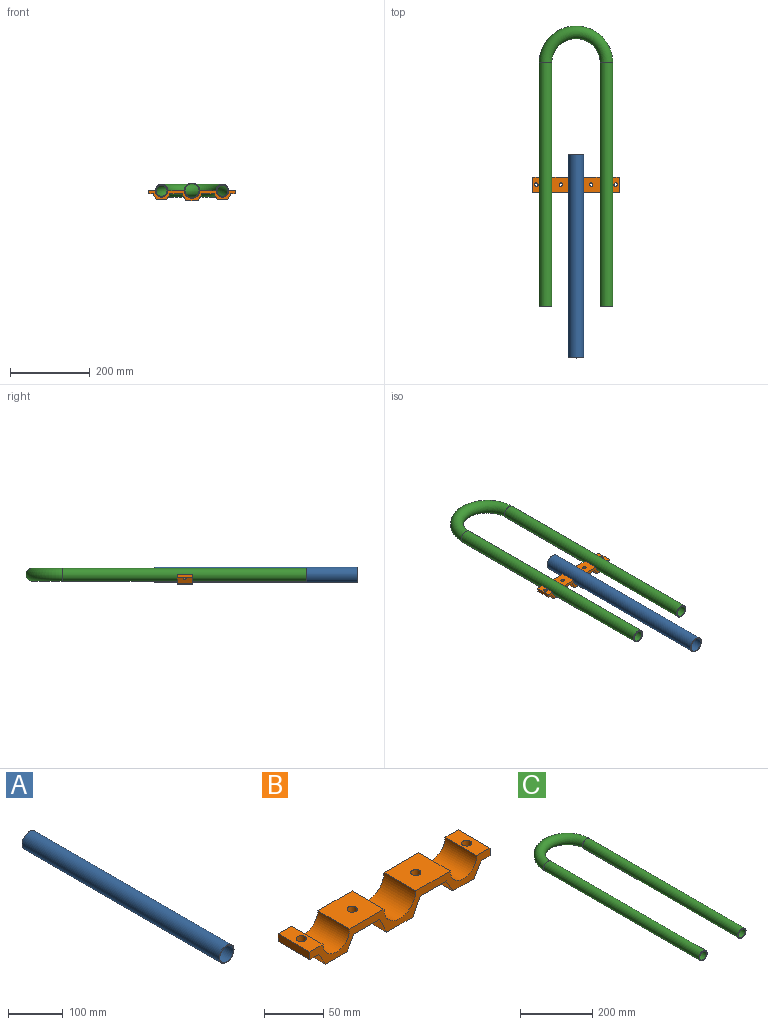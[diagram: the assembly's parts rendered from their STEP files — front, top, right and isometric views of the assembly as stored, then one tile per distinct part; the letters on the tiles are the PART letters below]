
ASSEMBLY  parts=3 mates=4
PART A: 4 faces, bbox 38.1x508x38.1 mm
  f0: cylinder r=17.58mm len=508mm, axis (0,1,0), area 56102.7mm2, adj f2,f3
  f1: cylinder r=19.05mm len=508mm, axis (0,1,0), area 60804.9mm2, adj f2,f3
  f2: plane 38.1x38.1mm, normal (0,-1,0), area 169.5mm2, adj f0,f1
  f3: plane 38.1x38.1mm, normal (0,1,0), area 169.5mm2, adj f0,f1
PART B: 28 faces, bbox 215.9x38.1x25.4 mm
  f0: plane 38.1x10.99mm, normal (0,0,-1), area 370.7mm2, adj f1,f4,f22,f23,f24
  f1: plane 38.1x14.29mm, normal (-0.87,0,-0.49), area 601.8mm2, adj f0,f5,f22,f23,f24
  f2: plane 38.1x14.29mm, normal (0.87,0,-0.49), area 601.8mm2, adj f3,f13,f22,f23,f27
  f3: plane 38.1x10.99mm, normal (0,0,-1), area 370.7mm2, adj f2,f14,f22,f23,f27
  f4: plane 38.1x7.94mm, normal (-1,0,0), area 302.4mm2, adj f0,f21,f22,f23
  f5: plane 38.1x25.4mm, normal (0,0,-1), area 967.7mm2, adj f1,f6,f22,f23
  f6: plane 38.1x14.29mm, normal (0.87,0,-0.49), area 625mm2, adj f5,f7,f22,f23
  f7: plane 38.1x31.31mm, normal (0,0,-1), area 1133.6mm2, adj f6,f8,f22,f23,f25
  f8: plane 38.1x17.46mm, normal (-0.9,0,-0.43), area 735.9mm2, adj f7,f9,f22,f23
  f9: plane 38.1x31.75mm, normal (0,0,-1), area 1209.7mm2, adj f8,f10,f22,f23
  f10: plane 38.1x17.46mm, normal (0.9,0,-0.43), area 735.9mm2, adj f9,f11,f22,f23
  f11: plane 38.1x31.31mm, normal (0,0,-1), area 1133.6mm2, adj f10,f12,f22,f23,f26
  f12: plane 38.1x14.29mm, normal (-0.87,0,-0.49), area 625mm2, adj f11,f13,f22,f23
  f13: plane 38.1x25.4mm, normal (0,0,-1), area 967.7mm2, adj f2,f12,f22,f23
  f14: plane 38.1x7.94mm, normal (1,0,0), area 302.4mm2, adj f3,f15,f22,f23
  f15: plane 38.1x15.88mm, normal (0,0,1), area 545.4mm2, adj f14,f16,f22,f23,f27
  f16: cylinder r=15.88mm len=38.1mm, axis (0,1,0), area 1900.2mm2, adj f15,f17,f22,f23
  f17: plane 41.28x38.1mm, normal (0,0,1), area 1513.1mm2, adj f16,f18,f22,f23,f26
  f18: cylinder r=19.05mm len=38.1mm, axis (0,1,0), area 2280.2mm2, adj f17,f19,f22,f23
  f19: plane 41.28x38.1mm, normal (0,0,1), area 1513.1mm2, adj f18,f20,f22,f23,f25
  f20: cylinder r=15.88mm len=38.1mm, axis (0,1,0), area 1900.2mm2, adj f19,f21,f22,f23
  f21: plane 38.1x15.88mm, normal (0,0,1), area 545.4mm2, adj f4,f20,f22,f23,f24
  f22: plane 215.9x25.4mm, normal (0,-1,0), area 2006.6mm2, adj f0,f1,f2,f3,f4,f5,f6,f7
  f23: plane 215.9x25.4mm, normal (0,1,0), area 2006.6mm2, adj f0,f1,f2,f3,f4,f5,f6,f7
  f24: cylinder r=4.35mm len=11.74mm, axis (0,0,1), area 239.5mm2, adj f0,f1,f21
  f25: cylinder r=4.35mm len=8.7mm, axis (0,0,1), area 216.9mm2, adj f7,f19
  f26: cylinder r=4.35mm len=8.7mm, axis (0,0,1), area 216.9mm2, adj f11,f17
  f27: cylinder r=4.35mm len=11.76mm, axis (0,0,1), area 239.5mm2, adj f2,f3,f15
PART C: 8 faces, bbox 199.3x709.3x31.8 mm
  f0: cylinder r=13.82mm len=609.6mm, axis (0,1,0), area 52924.6mm2, adj f1,f3
  f1: torus R=76.2mm, axis (0,0,-1), area 20783.4mm2, adj f0,f2
  f2: cylinder r=13.82mm len=609.6mm, axis (0,-1,0), area 52924.6mm2, adj f1,f4
  f3: plane 31.75x31.75mm, normal (0,-1,0), area 191.9mm2, adj f0,f5
  f4: plane 31.75x31.75mm, normal (0,-1,0), area 191.9mm2, adj f2,f7
  f5: cylinder r=15.88mm len=609.6mm, axis (0,1,0), area 60804.9mm2, adj f3,f6
  f6: torus R=76.2mm, axis (0,0,-1), area 23878mm2, adj f5,f7
  f7: cylinder r=15.88mm len=609.6mm, axis (0,-1,0), area 60804.9mm2, adj f4,f6
PLACE A t=(-6.86,0,14.11)mm
PLACE B t=(-6.86,198.68,14.11)mm fixed
PLACE C t=(-6.86,-125.17,14.11)mm
MATE cylindrical A.f1 <-> B.f18  axis (0,1,0) through (-6.86,0,14.11)mm
MATE cylindrical B.f20 <-> B.f24  axis (0,1,0) through (-83.06,198.68,14.11)mm
MATE cylindrical B.f16 <-> C.f7  axis (0,1,0) through (69.34,179.63,14.11)mm
MATE cylindrical C.f5 <-> B.f20  axis (0,1,0) through (-83.06,179.63,14.11)mm
